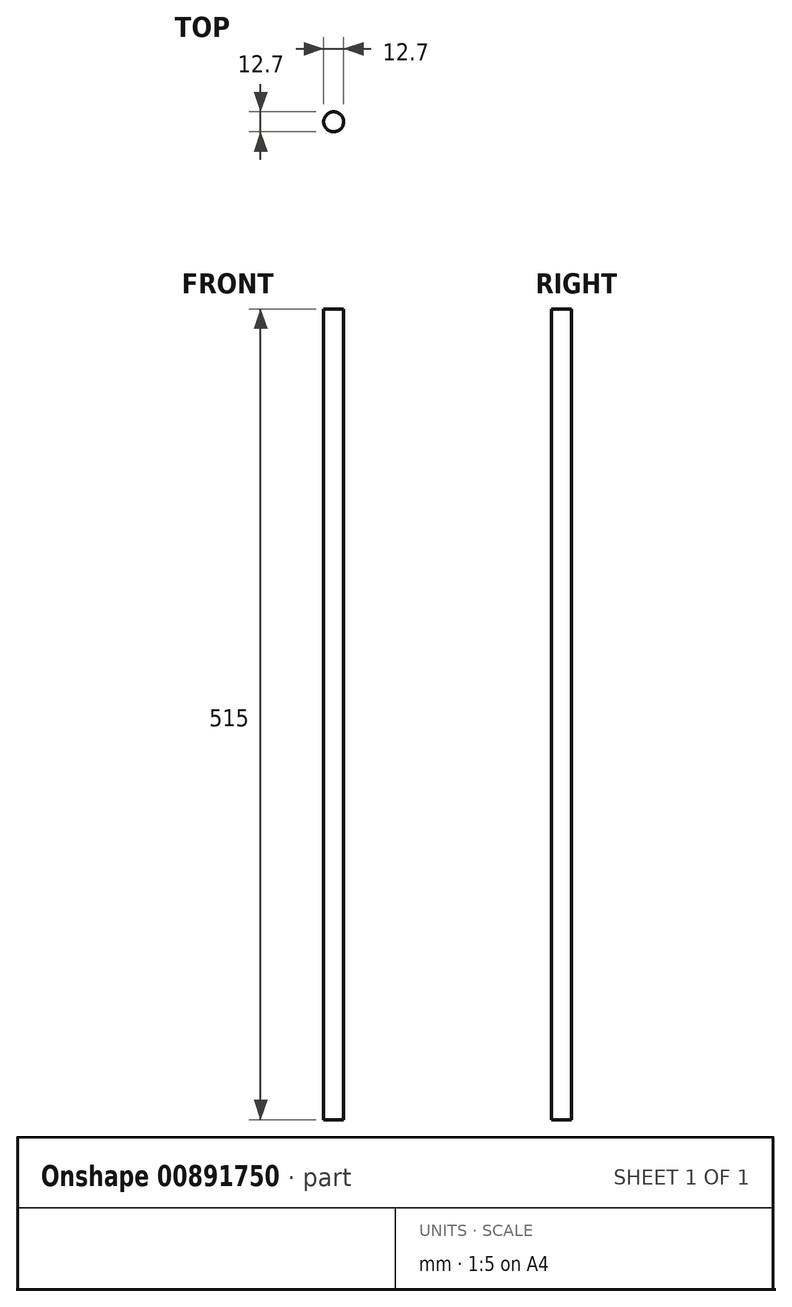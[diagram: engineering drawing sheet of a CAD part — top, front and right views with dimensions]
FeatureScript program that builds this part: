
annotation { "Feature Type Name" : "Feature", "Feature Type Description" : "" }
export const myFeature = defineFeature(function(context is Context, id is Id, definition is map)
    precondition{}
    {
        {
            var Q0;
            Q0=qCreatedBy(makeId("Top.planeOp"),FACE);
            var sketch = newSketch(context, id + "F0", { "sketchPlane" : qUnion([Q0])});
            skCircle(sketch, "E0", {"center": v(0, 0) * mm, "radius": 6.35 * mm});
            skSolve(sketch);
        }
        {
            var Q0;
            Q0=makeQuery(id+"F0.imprint","IMPRINT",FACE,{"disambiguationData":[TD([[makeQuery(id+"F0.imprint","IMPRINT",EDGE,{"derivedFrom":sQuery(id+"F0.wireOp",EDGE,"E0")}),1.0]])]});
            extrude(context, id + "F1", {"entities" : qUnion([Q0]), "depth" : 515 * mm, "offsetDistance" : 25.4 * mm});
        }
    });
